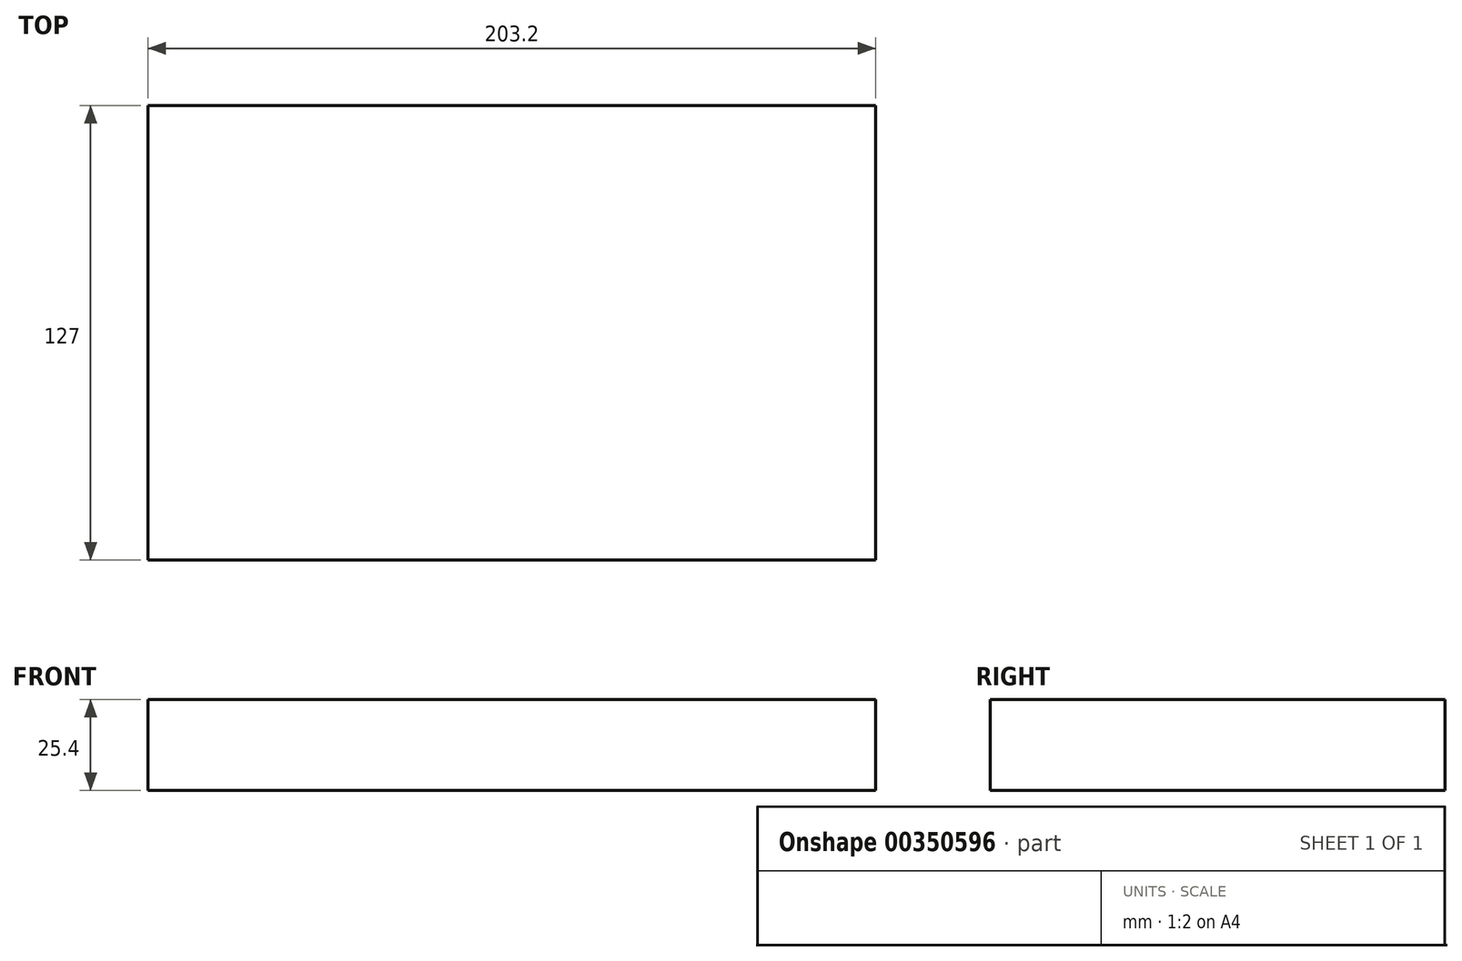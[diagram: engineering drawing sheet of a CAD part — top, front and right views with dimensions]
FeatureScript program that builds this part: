
annotation { "Feature Type Name" : "Feature", "Feature Type Description" : "" }
export const myFeature = defineFeature(function(context is Context, id is Id, definition is map)
    precondition{}
    {
        {
            var Q0;
            Q0=qCreatedBy(makeId("Front.planeOp"),FACE);
            var sketch = newSketch(context, id + "F0", { "sketchPlane" : qUnion([Q0])});
            skLineSegment(sketch, "E0.bottom", {"start": v(-102.67, 0) * mm, "end": v(100.53, 0) * mm});
            skLineSegment(sketch, "E0.top", {"start": v(-102.67, -25.4) * mm, "end": v(100.53, -25.4) * mm});
            skLineSegment(sketch, "E0.left", {"start": v(-102.67, 0) * mm, "end": v(-102.67, -25.4) * mm});
            skLineSegment(sketch, "E0.right", {"start": v(100.53, 0) * mm, "end": v(100.53, -25.4) * mm});
            skPoint(sketch, "E1", {"position": v(-45.52, 0) * mm});
            skPoint(sketch, "E2", {"position": v(43.38, 0) * mm});
            skSolve(sketch);
        }
        {
            var Q0;
            Q0=makeQuery(id+"F0.imprint","IMPRINT",FACE,{"disambiguationData":[TD([[makeQuery(id+"F0.imprint","IMPRINT",EDGE,{"derivedFrom":sQuery(id+"F0.wireOp",EDGE,"E0.bottom")}),-1.0]])]});
            extrude(context, id + "F1", {"entities" : qUnion([Q0]), "endBound" : BoundingType.SYMMETRIC, "depth" : 127 * mm});
        }
    });
